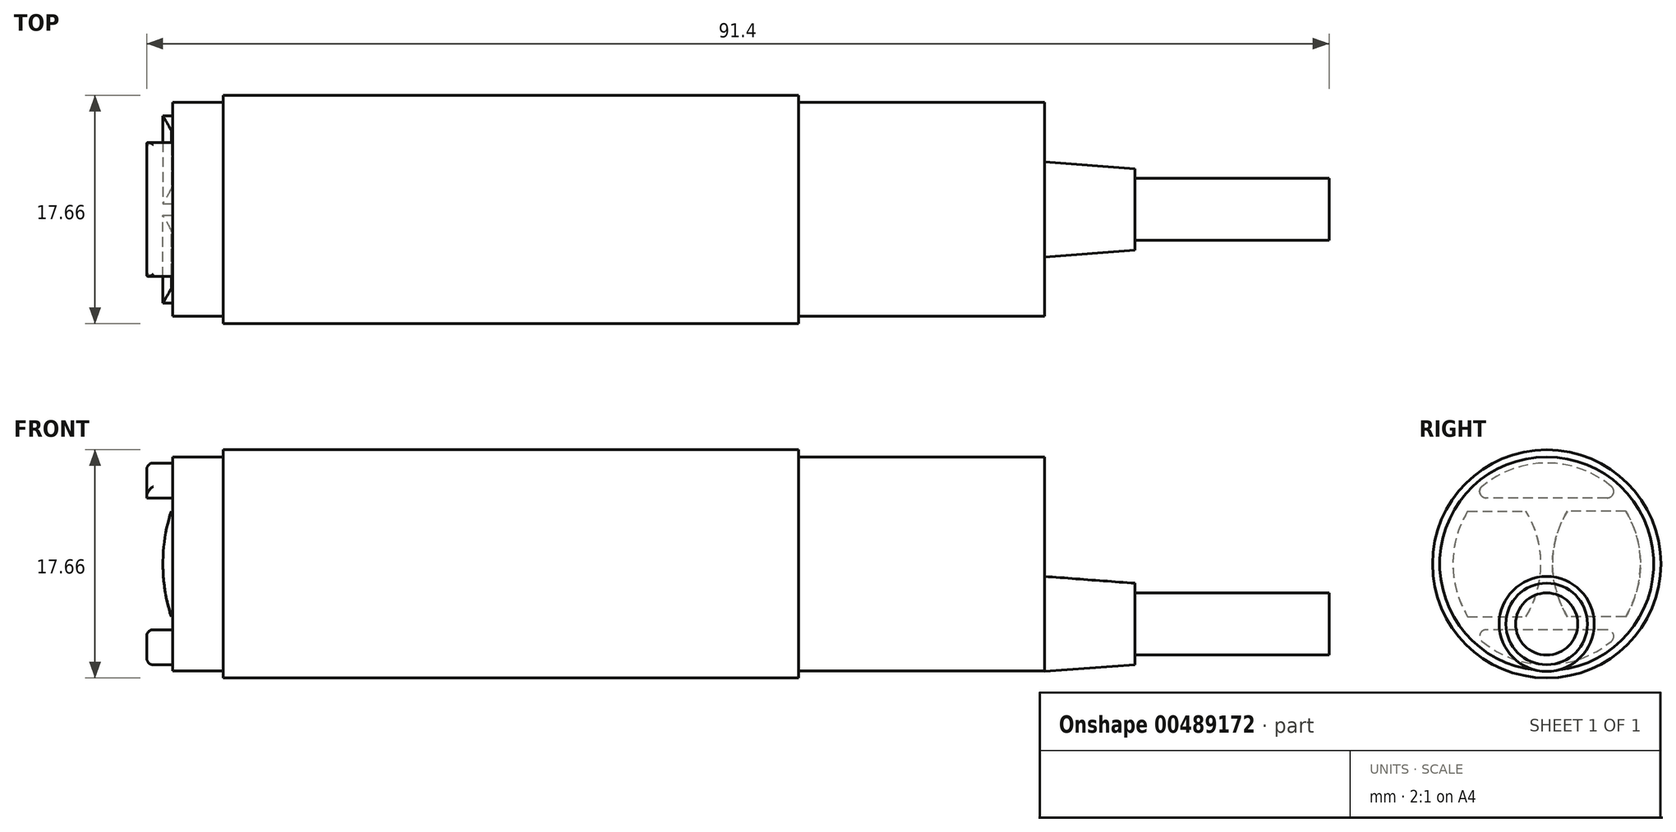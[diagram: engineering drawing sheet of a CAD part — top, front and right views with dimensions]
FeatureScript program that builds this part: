
annotation { "Feature Type Name" : "Feature", "Feature Type Description" : "" }
export const myFeature = defineFeature(function(context is Context, id is Id, definition is map)
    precondition{}
    {
        {
            var Q0;
            Q0=qCreatedBy(makeId("Front.planeOp"),FACE);
            var sketch = newSketch(context, id + "F0", { "sketchPlane" : qUnion([Q0])});
            skLineSegment(sketch, "E0", {"start": v(-69.4, 0) * mm, "end": v(-69.4, 7.8) * mm});
            skLineSegment(sketch, "E1", {"start": v(-69.4, 7.8) * mm, "end": v(-67.4, 7.8) * mm});
            skLineSegment(sketch, "E2", {"start": v(-67.4, 7.8) * mm, "end": v(-67.4, 8.27) * mm});
            skLineSegment(sketch, "E3", {"start": v(-67.4, 8.27) * mm, "end": v(-63.5, 8.27) * mm});
            skLineSegment(sketch, "E4", {"start": v(-63.5, 8.27) * mm, "end": v(-63.5, 8.82) * mm});
            skLineSegment(sketch, "E5", {"start": v(-63.5, 8.82) * mm, "end": v(-19, 8.82) * mm});
            skLineSegment(sketch, "E6", {"start": v(-19, 8.82) * mm, "end": v(-19, 8.27) * mm});
            skLineSegment(sketch, "E7", {"start": v(-19, 8.27) * mm, "end": v(0, 8.27) * mm});
            skLineSegment(sketch, "E8", {"start": v(0, 8.27) * mm, "end": v(0, 0) * mm});
            skLineSegment(sketch, "E9", {"start": v(0, 0) * mm, "end": v(-69.4, 0) * mm});
            skSolve(sketch);
        }
        {
            var Q0;
            Q0=makeQuery(id+"F0.imprint","IMPRINT",FACE,{"disambiguationData":[TD([[makeQuery(id+"F0.imprint","IMPRINT",EDGE,{"derivedFrom":sQuery(id+"F0.wireOp",EDGE,"E0")}),-1.0]])]});
            var Q1;
            Q1=sQuery(id+"F0.wireOp",EDGE,"E9");
            revolve(context, id + "F1", {"entities" : qUnion([Q0]), "axis" : qUnion([Q1]), "revolveType" : RevolveType.FULL});
        }
        {
            var Q0;
            Q0=qCreatedBy(makeId("Front.planeOp"),FACE);
            var sketch = newSketch(context, id + "F2", { "sketchPlane" : qUnion([Q0])});
            skLineSegment(sketch, "E10.bottom", {"start": v(-69.4, 5.1) * mm, "end": v(-67.4, 5.1) * mm});
            skLineSegment(sketch, "E10.top", {"start": v(-69.4, -5.1) * mm, "end": v(-67.4, -5.1) * mm});
            skLineSegment(sketch, "E10.left", {"start": v(-69.4, 5.1) * mm, "end": v(-69.4, -5.1) * mm});
            skLineSegment(sketch, "E10.right", {"start": v(-67.4, 5.1) * mm, "end": v(-67.4, -5.1) * mm});
            skSolve(sketch);
        }
        {
            var Q0;
            Q0 = qSketchRegion(id + "F2", true);
            extrude(context, id + "F3", {"entities" : qUnion([Q0]), "operationType" : NewBodyOperationType.REMOVE, "endBound" : BoundingType.SYMMETRIC, "oppositeDirection" : true, "depth" : 25 * mm});
        }
        {
            var Q0;
            Q0=makeQuery(id+"F3.boolean.opBoolean","COPY",EDGE,{"derivedFrom":makeQuery(id+"F3.opExtrude","SWEPT_EDGE",EDGE,{"disambiguationData":[OSD([sQuery(id+"F2.wireOp",EDGE,"E10.bottom"),sQuery(id+"F2.wireOp",EDGE,"E10.left")])]})});
            var Q1;
            Q1=makeQuery(id+"F3.boolean.opBoolean","INTERSECT",EDGE,{"disambiguationData":[OD(0.0)],"derivedFrom":[makeQuery(id+"F1.opRevolve","SWEPT_FACE",FACE,{"disambiguationData":[OSD([sQuery(id+"F0.wireOp",EDGE,"E1")])]}),makeQuery(id+"F3.opExtrude","SWEPT_FACE",FACE,{"disambiguationData":[OSD([sQuery(id+"F2.wireOp",EDGE,"E10.bottom")])]})]});
            var Q2;
            {var subQ0=sQuery(id+"F0.wireOp",EDGE,"E0");var subQ1=sQuery(id+"F0.wireOp",EDGE,"E1");Q2=makeQuery(id+"F3.boolean.opBoolean","SPLIT",EDGE,{"disambiguationData":[TD([makeQuery(id+"F3.opExtrude","SWEPT_FACE",FACE,{"disambiguationData":[OSD([sQuery(id+"F2.wireOp",EDGE,"E10.bottom")])]})])],"derivedFrom":makeQuery(id+"F1.opRevolve","SWEPT_EDGE",EDGE,{"disambiguationData":[OSD([subQ0,subQ1])]})});}
            var Q3;
            Q3=makeQuery(id+"F3.boolean.opBoolean","INTERSECT",EDGE,{"disambiguationData":[OD(1.0)],"derivedFrom":[makeQuery(id+"F1.opRevolve","SWEPT_FACE",FACE,{"disambiguationData":[OSD([sQuery(id+"F0.wireOp",EDGE,"E1")])]}),makeQuery(id+"F3.opExtrude","SWEPT_FACE",FACE,{"disambiguationData":[OSD([sQuery(id+"F2.wireOp",EDGE,"E10.bottom")])]})]});
            var Q4;
            Q4=makeQuery(id+"F3.boolean.opBoolean","INTERSECT",EDGE,{"disambiguationData":[OD(1.0)],"derivedFrom":[makeQuery(id+"F1.opRevolve","SWEPT_FACE",FACE,{"disambiguationData":[OSD([sQuery(id+"F0.wireOp",EDGE,"E1")])]}),makeQuery(id+"F3.opExtrude","SWEPT_FACE",FACE,{"disambiguationData":[OSD([sQuery(id+"F2.wireOp",EDGE,"E10.top")])]})]});
            var Q5;
            Q5=makeQuery(id+"F3.boolean.opBoolean","INTERSECT",EDGE,{"disambiguationData":[OD(0.0)],"derivedFrom":[makeQuery(id+"F1.opRevolve","SWEPT_FACE",FACE,{"disambiguationData":[OSD([sQuery(id+"F0.wireOp",EDGE,"E1")])]}),makeQuery(id+"F3.opExtrude","SWEPT_FACE",FACE,{"disambiguationData":[OSD([sQuery(id+"F2.wireOp",EDGE,"E10.top")])]})]});
            var Q6;
            {var subQ0=sQuery(id+"F0.wireOp",EDGE,"E0");var subQ1=sQuery(id+"F0.wireOp",EDGE,"E1");Q6=makeQuery(id+"F3.boolean.opBoolean","SPLIT",EDGE,{"disambiguationData":[TD([makeQuery(id+"F3.opExtrude","SWEPT_FACE",FACE,{"disambiguationData":[OSD([sQuery(id+"F2.wireOp",EDGE,"E10.top")])]})])],"derivedFrom":makeQuery(id+"F1.opRevolve","SWEPT_EDGE",EDGE,{"disambiguationData":[OSD([subQ0,subQ1])]})});}
            var Q7;
            Q7=makeQuery(id+"F3.boolean.opBoolean","COPY",EDGE,{"derivedFrom":makeQuery(id+"F3.opExtrude","SWEPT_EDGE",EDGE,{"disambiguationData":[OSD([sQuery(id+"F2.wireOp",EDGE,"E10.top"),sQuery(id+"F2.wireOp",EDGE,"E10.left")])]})});
            fillet(context, id + "F4", {"entities" : qUnion([Q0, Q1, Q2, Q3, Q4, Q5, Q6, Q7]), "radius" : 0.5 * mm, "tangentPropagation" : true, "allowEdgeOverflow" : false});
        }
        {
            var Q0;
            Q0=qCreatedBy(makeId("Top.planeOp"),FACE);
            cPlane(context, id + "F5", {"entities" : qUnion([Q0]), "cplaneType" : CPlaneType.OFFSET, "offset" : 4.65 * mm, "oppositeDirection" : true, "width" : 150 * mm, "height" : 150 * mm});
        }
        {
            var Q0;
            Q0=qCreatedBy(id+"F5.planeOp",FACE);
            var sketch = newSketch(context, id + "F6", { "sketchPlane" : qUnion([Q0])});
            skLineSegment(sketch, "E11", {"start": v(0, -3.67) * mm, "end": v(7, -3.15) * mm});
            skLineSegment(sketch, "E12", {"start": v(7, -3.15) * mm, "end": v(7, 0) * mm});
            skLineSegment(sketch, "E13", {"start": v(0, 0) * mm, "end": v(7, 0) * mm});
            skLineSegment(sketch, "E14", {"start": v(0, -3.67) * mm, "end": v(0, 0) * mm});
            skSolve(sketch);
        }
        {
            var Q0;
            Q0=makeQuery(id+"F6.imprint","IMPRINT",FACE,{"disambiguationData":[TD([[makeQuery(id+"F6.imprint","IMPRINT",EDGE,{"derivedFrom":sQuery(id+"F6.wireOp",EDGE,"E11")}),1.0]])]});
            var Q1;
            Q1=sQuery(id+"F6.wireOp",EDGE,"E13");
            revolve(context, id + "F7", {"entities" : qUnion([Q0]), "axis" : qUnion([Q1]), "revolveType" : RevolveType.FULL});
        }
        {
            var Q0;
            Q0=qCreatedBy(id+"F5.planeOp",FACE);
            var sketch = newSketch(context, id + "F8", { "sketchPlane" : qUnion([Q0])});
            skLineSegment(sketch, "E15.bottom", {"start": v(7, 0) * mm, "end": v(22, 0) * mm});
            skLineSegment(sketch, "E15.top", {"start": v(7, 2.4) * mm, "end": v(22, 2.4) * mm});
            skLineSegment(sketch, "E15.left", {"start": v(7, 0) * mm, "end": v(7, 2.4) * mm});
            skLineSegment(sketch, "E15.right", {"start": v(22, 0) * mm, "end": v(22, 2.4) * mm});
            skSolve(sketch);
        }
        {
            var Q0;
            Q0 = qSketchRegion(id + "F8", true);
            var Q1;
            Q1=sQuery(id+"F8.wireOp",EDGE,"E15.bottom");
            revolve(context, id + "F9", {"entities" : qUnion([Q0]), "axis" : qUnion([Q1]), "revolveType" : RevolveType.FULL});
        }
        {
            var Q0;
            Q0=makeQuery(id+"F3.boolean.opBoolean","MERGE",FACE,{"derivedFrom":[makeQuery(id+"F1.opRevolve","SWEPT_FACE",FACE,{"disambiguationData":[OSD([sQuery(id+"F0.wireOp",EDGE,"E2")])]}),makeQuery(id+"F3.opExtrude","SWEPT_FACE",FACE,{"disambiguationData":[OSD([sQuery(id+"F2.wireOp",EDGE,"E10.right")])]})]});
            var sketch = newSketch(context, id + "F10", { "sketchPlane" : qUnion([Q0])});
            skArc(sketch, "E16", {"start": v(-6.1, 4.08) * mm, "mid": v(-7.25, 0) * mm, "end": v(-6.1, -4.08) * mm});
            skArc(sketch, "E17", {"start": v(-1.6, -4.08) * mm, "mid": v(-0.45, 0) * mm, "end": v(-1.6, 4.08) * mm});
            skLineSegment(sketch, "E18", {"start": v(-6.1, -4.08) * mm, "end": v(-1.6, -4.08) * mm});
            skLineSegment(sketch, "E19.MirrorCS", {"start": v(-6.1, 4.08) * mm, "end": v(-1.6, 4.08) * mm});
            skLineSegment(sketch, "E20", {"start": v(-3.85, 4.08) * mm, "end": v(-3.85, -4.08) * mm, "construction": true});
            skSolve(sketch);
        }
        {
            var Q0;
            Q0=makeQuery(id+"F10.imprint","IMPRINT",FACE,{"disambiguationData":[TD([[makeQuery(id+"F10.imprint","IMPRINT",EDGE,{"derivedFrom":sQuery(id+"F10.wireOp",EDGE,"E16")}),1.0]])]});
            extrude(context, id + "F11", {"entities" : qUnion([Q0]), "depth" : 0.75 * mm});
        }
        {
            var Q0;
            Q0=qCreatedBy(makeId("Front.planeOp"),FACE);
            var sketch = newSketch(context, id + "F12", { "sketchPlane" : qUnion([Q0])});
            skArc(sketch, "E21", {"start": v(-67.5, 4.08) * mm, "mid": v(-68.15, 0) * mm, "end": v(-67.5, -4.08) * mm});
            skPoint(sketch, "E22", {"position": v(-67.5, 4.08) * mm});
            skLineSegment(sketch, "E23.0", {"start": v(-68.15, 4.08) * mm, "end": v(-67.4, 4.08) * mm});
            skPoint(sketch, "E24.0", {"position": v(-67.78, -4.08) * mm});
            skLineSegment(sketch, "E25", {"start": v(-68.15, 4.08) * mm, "end": v(-68.15, 0) * mm});
            skLineSegment(sketch, "E26", {"start": v(-68.15, 0) * mm, "end": v(-68.15, -4.08) * mm});
            skLineSegment(sketch, "E27", {"start": v(-68.15, -4.08) * mm, "end": v(-67.5, -4.08) * mm});
            skSolve(sketch);
        }
        {
            var Q0;
            Q0 = qSketchRegion(id + "F12", true);
            extrude(context, id + "F13", {"entities" : qUnion([Q0]), "operationType" : NewBodyOperationType.REMOVE, "endBound" : BoundingType.THROUGH_ALL, "oppositeDirection" : true, "depth" : 25 * mm});
        }
        {
            var Q0;
            Q0=makeQuery(id+"F11.opExtrude","SWEPT_BODY",BODY,{"disambiguationData":[OSD([sQuery(id+"F10.wireOp",EDGE,"E16"),sQuery(id+"F10.wireOp",EDGE,"E17"),sQuery(id+"F10.wireOp",EDGE,"E18"),sQuery(id+"F10.wireOp",EDGE,"E19.MirrorCS")])]});
            var Q1;
            Q1=qCreatedBy(makeId("Front.planeOp"),FACE);
            mirror(context, id + "F14", {"operationType" : NewBodyOperationType.ADD, "entities" : qUnion([Q0]), "mirrorPlane" : qUnion([Q1])});
        }
    });
